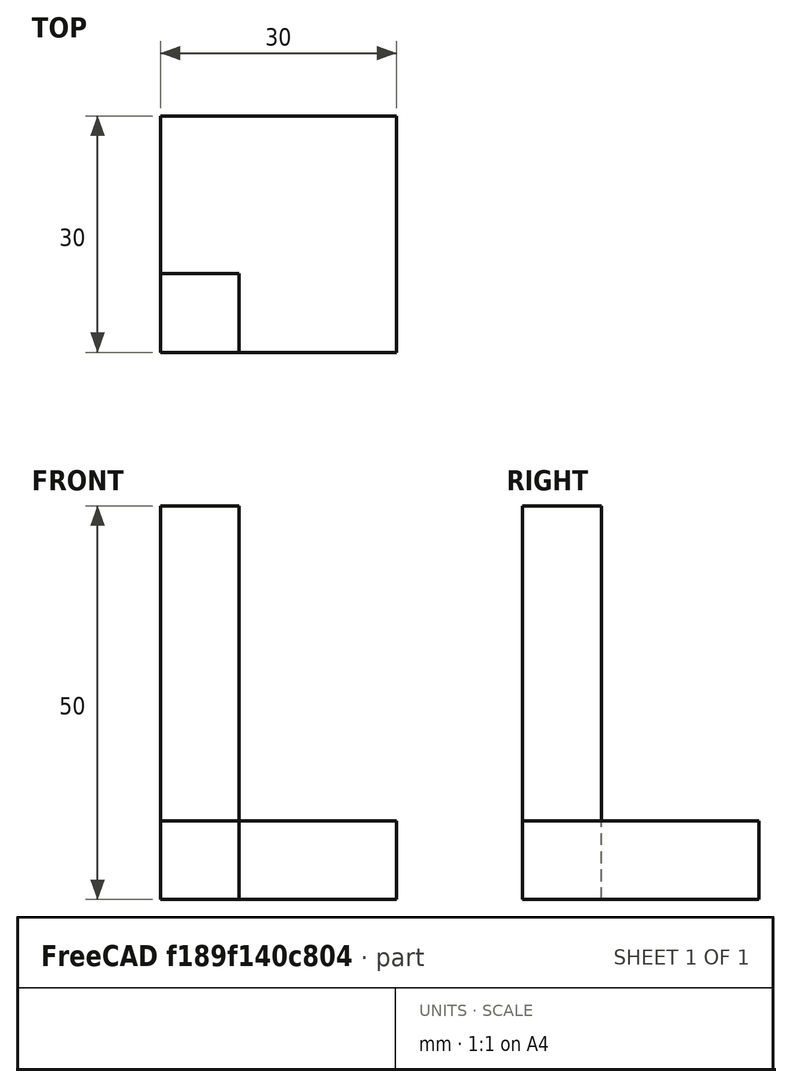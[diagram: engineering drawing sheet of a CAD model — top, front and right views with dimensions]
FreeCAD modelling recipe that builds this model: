
FCSTD DOCUMENT  (FreeCAD 0.14R3702 (Git))
Label: cubos-1
License: CC-BY 3.0
LicenseURL: http://creativecommons.org/licenses/by/3.0/
objects: App::MeasureDistance×4, Part::Box×2
note: 2 computed .brp shape members not serialized (recipe doc carries the construction recipe); baked Part::Feature solids carry a one-line shape summary decoded from their .brp

FEATURE [Part::Box] Box  label="Cubo"
  Height = 10
  Length = 30
  Width = 30
FEATURE [Part::Box] Box001  label="Cubo001"
  Height = 50
  Length = 10
  Width = 10
FEATURE [App::MeasureDistance] Distance  label="Distance: 50.002"
  Distance = 50.0023
  P1 = (0.675731,0,50)
  P2 = (0.199297,0,0)
FEATURE [App::MeasureDistance] Distance003  label="Distance: 10.000"
  Distance = 10.0005
  P1 = (30,29.9038,10)
  P2 = (30,30,0)
FEATURE [App::MeasureDistance] Distance004  label="Distance: 10.001"
  Distance = 10
  P1 = (10,0,50)
  P2 = (10,10,50)
FEATURE [App::MeasureDistance] Distance005  label="Distance: 30.000"
  Distance = 30
  P1 = (0,0,10)
  P2 = (30,0,10)
